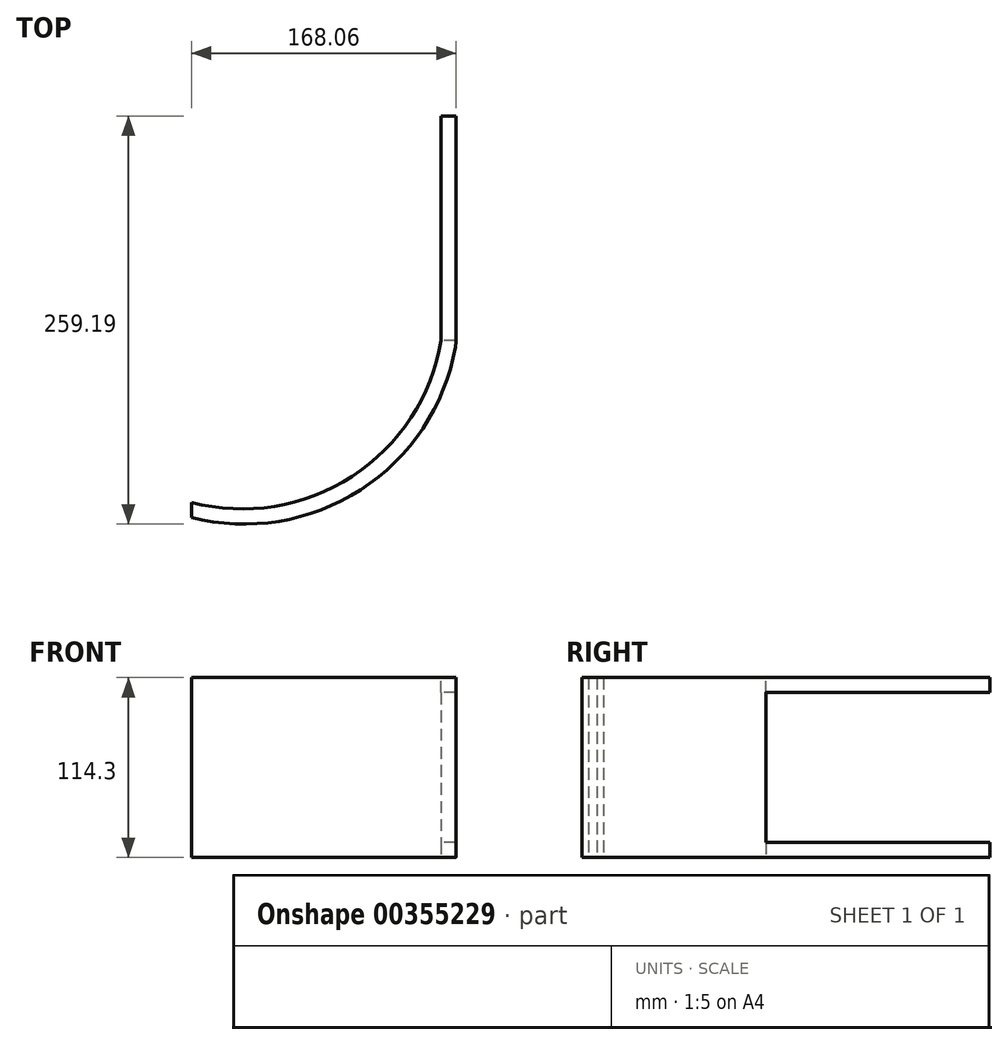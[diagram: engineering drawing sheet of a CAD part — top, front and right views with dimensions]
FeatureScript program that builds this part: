
annotation { "Feature Type Name" : "Feature", "Feature Type Description" : "" }
export const myFeature = defineFeature(function(context is Context, id is Id, definition is map)
    precondition{}
    {
        {
            var Q0;
            Q0=qCreatedBy(makeId("Top.planeOp"),FACE);
            var sketch = newSketch(context, id + "F0", { "sketchPlane" : qUnion([Q0])});
            skLineSegment(sketch, "E0", {"start": v(0, -40.85) * mm, "end": v(0, 101.6) * mm});
            skArc(sketch, "E1", {"start": v(-168.06, -153.37) * mm, "mid": v(-60.66, -135.89) * mm, "end": v(-0.4, -45.3) * mm});
            skPoint(sketch, "E2.visualSharp", {"position": v(0, 0) * mm});
            skArc(sketch, "E2.filletArc", {"start": v(-0.4, -45.3) * mm, "mid": v(-0.1, -43.08) * mm, "end": v(0, -40.85) * mm});
            skLineSegment(sketch, "E3", {"start": v(0, 101.6) * mm, "end": v(-76.2, 101.6) * mm});
            skLineSegment(sketch, "E4", {"start": v(-76.2, 101.6) * mm, "end": v(-76.2, 1.78) * mm});
            skLineSegment(sketch, "E5", {"start": v(-168.06, -153.37) * mm, "end": v(-168.06, -77.17) * mm});
            skArc(sketch, "E6", {"start": v(-168.06, -77.17) * mm, "mid": v(-107.9, -57.16) * mm, "end": v(-76.5, -2.08) * mm});
            skPoint(sketch, "E7.visualSharp", {"position": v(-76.2, 0) * mm});
            skArc(sketch, "E7.filletArc", {"start": v(-76.5, -2.08) * mm, "mid": v(-76.27, -0.16) * mm, "end": v(-76.2, 1.78) * mm});
            skLineSegment(sketch, "E8.bottom", {"start": v(0, 101.6) * mm, "end": v(-9.53, 101.6) * mm});
            skLineSegment(sketch, "E8.top", {"start": v(0, -40.89) * mm, "end": v(-9.52, -40.89) * mm});
            skLineSegment(sketch, "E8.left", {"start": v(0, 101.6) * mm, "end": v(0, -40.89) * mm});
            skLineSegment(sketch, "E8.right", {"start": v(-9.53, 101.6) * mm, "end": v(-9.52, -40.89) * mm});
            skArc(sketch, "E9", {"start": v(-168.06, -143.84) * mm, "mid": v(-66.07, -127.35) * mm, "end": v(-9.52, -40.89) * mm});
            skSolve(sketch);
        }
        {
            var Q0;
            Q0=makeQuery(id+"F0.imprint","IMPRINT",FACE,{"disambiguationData":[TD([[makeQuery(id+"F0.imprint","IMPRINT",EDGE,{"derivedFrom":sQuery(id+"F0.wireOp",EDGE,"E3")}),1.0]])]});
            extrude(context, id + "F1", {"entities" : qUnion([Q0]), "depth" : 9.52 * mm});
        }
        {
            var Q0;
            Q0=makeQuery(id+"F0.imprint","IMPRINT",FACE,{"disambiguationData":[TD([[makeQuery(id+"F0.imprint","IMPRINT",EDGE,{"derivedFrom":sQuery(id+"F0.wireOp",EDGE,"E8.bottom")}),1.0]])]});
            var Q1;
            {var subQ1=sQuery(id+"F0.wireOp",EDGE,"E1");Q1=makeQuery(id+"F0.imprint","IMPRINT",FACE,{"disambiguationData":[TD([[makeQuery(id+"F0.imprint","IMPRINT",EDGE,{"derivedFrom":subQ1}),1.0]])]});}
            extrude(context, id + "F2", {"entities" : qUnion([Q0, Q1]), "operationType" : NewBodyOperationType.ADD, "depth" : 57.15 * mm});
        }
        {
            var Q0;
            Q0=makeQuery(id+"F1.opExtrude","SWEPT_BODY",BODY,{"disambiguationData":[OSD([sQuery(id+"F0.wireOp",EDGE,"E3"),sQuery(id+"F0.wireOp",EDGE,"E4"),sQuery(id+"F0.wireOp",EDGE,"E5"),sQuery(id+"F0.wireOp",EDGE,"E6"),sQuery(id+"F0.wireOp",EDGE,"E7.filletArc"),sQuery(id+"F0.wireOp",EDGE,"E8.right"),sQuery(id+"F0.wireOp",EDGE,"E9")])]});
            var Q1;
            Q1=makeQuery(id+"F2.opExtrude","CAP_FACE",FACE,{"disambiguationData":[OSD([sQuery(id+"F0.wireOp",EDGE,"E1"),sQuery(id+"F0.wireOp",EDGE,"E2.filletArc"),sQuery(id+"F0.wireOp",EDGE,"E5"),sQuery(id+"F0.wireOp",EDGE,"E8.bottom"),sQuery(id+"F0.wireOp",EDGE,"E8.left"),sQuery(id+"F0.wireOp",EDGE,"E8.right"),sQuery(id+"F0.wireOp",EDGE,"E9")])],"isStart":false});
            mirror(context, id + "F3", {"operationType" : NewBodyOperationType.ADD, "entities" : qUnion([Q0]), "mirrorPlane" : qUnion([Q1])});
        }
    });
